FCSTD DOCUMENT  (FreeCAD 0.21R33771 (Git))
Label: RING2
License: All rights reserved
LicenseURL: http://en.wikipedia.org/wiki/All_rights_reserved
objects: Part::Part2DObjectPython×168, App::FeaturePython×24, App::DocumentObjectGroup×1
note: 168 computed .brp shape members not serialized (recipe doc carries the construction recipe); baked Part::Feature solids carry a one-line shape summary decoded from their .brp

FEATURE [Part::Part2DObjectPython] Rectangle  # Draft 2D object (typed FeaturePython)
  Area = 0
  ChamferSize = 0
  Columns = 1
  FilletRadius = 0
  Height = 6
  Length = 6
  MakeFace = false
  Placement = pos=(269.144,-43.1167,0) rot=(0,0,1;4.70122rad)
  Rows = 1
FEATURE [App::FeaturePython] Text  # WARN: FeaturePython — macro-defined, semantics opaque (R4)
  Placement = pos=(270.79,-53.3517,0) rot=(0,0,-1;4.73892rad)
  Text = 2
FEATURE [App::FeaturePython] Text001  # WARN: FeaturePython — macro-defined, semantics opaque (R4)
  Placement = pos=(268.047,49.5386,0) rot=(0,0,1;2.6241rad)
  Text = 6.
FEATURE [Part::Part2DObjectPython] Circle  # Draft 2D object (typed FeaturePython)
  Area = 1.13097
  FirstAngle = 0
  LastAngle = 0
  MakeFace = true
  Placement = pos=(272.07,-49.7498,0) rot=(0,0,1;4.70122rad)
  Radius = 0.6
FEATURE [Part::Part2DObjectPython] Rectangle001  # Draft 2D object (typed FeaturePython)
  Area = 0
  ChamferSize = 0
  Columns = 1
  FilletRadius = 0
  Height = 6
  Length = 6
  MakeFace = false
  Placement = pos=(270.385,-29.144,0) rot=(0,0,1;5.08397rad)
  Rows = 1
FEATURE [Part::Part2DObjectPython] Circle001  # Draft 2D object (typed FeaturePython)
  Area = 1.13097
  FirstAngle = 0
  LastAngle = 0
  MakeFace = true
  Placement = pos=(275.577,-34.2043,0) rot=(0,0,1;5.08397rad)
  Radius = 0.6
FEATURE [Part::Part2DObjectPython] Rectangle002  # Draft 2D object (typed FeaturePython)
  Area = 0
  ChamferSize = 0
  Columns = 1
  FilletRadius = 0
  Height = 6
  Length = 6
  MakeFace = false
  Placement = pos=(271.331,-15.2783,0) rot=(0,0,1;5.4573rad)
  Rows = 1
FEATURE [Part::Part2DObjectPython] Circle002  # Draft 2D object (typed FeaturePython)
  Area = 1.13097
  FirstAngle = 0
  LastAngle = 0
  MakeFace = true
  Placement = pos=(278.01,-18.0965,0) rot=(0,0,1;5.4573rad)
  Radius = 0.6
FEATURE [Part::Part2DObjectPython] Rectangle003  # Draft 2D object (typed FeaturePython)
  Area = 0
  ChamferSize = 0
  Columns = 1
  FilletRadius = 0
  Height = 6
  Length = 6
  MakeFace = false
  Placement = pos=(271.89,-1.0508,0) rot=(0,0,1;5.74807rad)
  Rows = 1
FEATURE [Part::Part2DObjectPython] Circle003  # Draft 2D object (typed FeaturePython)
  Area = 1.13097
  FirstAngle = 0
  LastAngle = 0
  MakeFace = true
  Placement = pos=(279.097,-1.83579,0) rot=(0,0,1;5.74807rad)
  Radius = 0.6
FEATURE [Part::Part2DObjectPython] Rectangle004  # Draft 2D object (typed FeaturePython)
  Area = 0
  ChamferSize = 0
  Columns = 1
  FilletRadius = 0
  Height = 6
  Length = 6
  MakeFace = false
  Placement = pos=(271.77,13.5629,0) rot=(0,0,1;5.95873rad)
  Rows = 1
FEATURE [Part::Part2DObjectPython] Circle004  # Draft 2D object (typed FeaturePython)
  Area = 1.13097
  FirstAngle = 0
  LastAngle = 0
  MakeFace = true
  Placement = pos=(278.982,14.3023,0) rot=(0,0,1;5.95873rad)
  Radius = 0.6
FEATURE [Part::Part2DObjectPython] Rectangle005  # Draft 2D object (typed FeaturePython)
  Area = 0
  ChamferSize = 0
  Columns = 1
  FilletRadius = 0
  Height = 6
  Length = 6
  MakeFace = false
  Placement = pos=(270.817,28.3851,0) rot=(0,0,1;6.11773rad)
  Rows = 1
FEATURE [Part::Part2DObjectPython] Circle005  # Draft 2D object (typed FeaturePython)
  Area = 1.13097
  FirstAngle = 0
  LastAngle = 0
  MakeFace = true
  Placement = pos=(277.821,30.2571,0) rot=(0,0,1;6.11773rad)
  Radius = 0.6
FEATURE [Part::Part2DObjectPython] Rectangle006  # Draft 2D object (typed FeaturePython)
  Area = 0
  ChamferSize = 0
  Columns = 1
  FilletRadius = 0
  Height = 6
  Length = 6
  MakeFace = false
  Placement = pos=(268.997,43.2674,0) rot=(0,0,1;6.24479rad)
  Rows = 1
FEATURE [Part::Part2DObjectPython] Circle006  # Draft 2D object (typed FeaturePython)
  Area = 1.13097
  FirstAngle = 0
  LastAngle = 0
  MakeFace = true
  Placement = pos=(275.707,46.0118,0) rot=(0,0,1;6.24479rad)
  Radius = 0.6
FEATURE [Part::Part2DObjectPython] Rectangle007  # Draft 2D object (typed FeaturePython)
  Area = 0
  ChamferSize = 0
  Columns = 1
  FilletRadius = 0
  Height = 6
  Length = 6
  MakeFace = false
  Placement = pos=(256.356,92.5739,0) rot=(0,0,1;0.191463rad)
  Rows = 1
FEATURE [App::FeaturePython] Text002  # WARN: FeaturePython — macro-defined, semantics opaque (R4)
  Placement = pos=(261.188,89.1931,0) rot=(0,0,-1;4.21532rad)
  Text = 2
FEATURE [App::FeaturePython] Text003  # WARN: FeaturePython — macro-defined, semantics opaque (R4)
  Placement = pos=(207.363,176.926,0) rot=(0,0,1;3.1477rad)
  Text = 7
FEATURE [Part::Part2DObjectPython] Circle007  # Draft 2D object (typed FeaturePython)
  Area = 1.13097
  FirstAngle = 0
  LastAngle = 0
  MakeFace = true
  Placement = pos=(262.264,96.7751,0) rot=(0,0,1;0.191463rad)
  Radius = 0.6
FEATURE [Part::Part2DObjectPython] Rectangle008  # Draft 2D object (typed FeaturePython)
  Area = 0
  ChamferSize = 0
  Columns = 1
  FilletRadius = 0
  Height = 6
  Length = 6
  MakeFace = false
  Placement = pos=(250.416,107.017,0) rot=(0,0,1;0.145211rad)
  Rows = 1
FEATURE [Part::Part2DObjectPython] Circle008  # Draft 2D object (typed FeaturePython)
  Area = 1.13097
  FirstAngle = 0
  LastAngle = 0
  MakeFace = true
  Placement = pos=(256.512,110.941,0) rot=(0,0,1;0.145211rad)
  Radius = 0.6
FEATURE [Part::Part2DObjectPython] Rectangle009  # Draft 2D object (typed FeaturePython)
  Area = 0
  ChamferSize = 0
  Columns = 1
  FilletRadius = 0
  Height = 6
  Length = 6
  MakeFace = false
  Placement = pos=(243.301,121.481,0) rot=(0,0,1;6.2598rad)
  Rows = 1
FEATURE [Part::Part2DObjectPython] Circle009  # Draft 2D object (typed FeaturePython)
  Area = 1.13097
  FirstAngle = 0
  LastAngle = 0
  MakeFace = true
  Placement = pos=(249.969,124.326,0) rot=(0,0,1;6.2598rad)
  Radius = 0.6
FEATURE [Part::Part2DObjectPython] Rectangle010  # Draft 2D object (typed FeaturePython)
  Area = 0
  ChamferSize = 0
  Columns = 1
  FilletRadius = 0
  Height = 6
  Length = 6
  MakeFace = false
  Placement = pos=(235.214,136.126,0) rot=(0,0,1;5.95541rad)
  Rows = 1
FEATURE [Part::Part2DObjectPython] Circle010  # Draft 2D object (typed FeaturePython)
  Area = 1.13097
  FirstAngle = 0
  LastAngle = 0
  MakeFace = true
  Placement = pos=(242.428,136.841,0) rot=(0,0,1;5.95541rad)
  Radius = 0.6
FEATURE [Part::Part2DObjectPython] Rectangle011  # Draft 2D object (typed FeaturePython)
  Area = 0
  ChamferSize = 0
  Columns = 1
  FilletRadius = 0
  Height = 6
  Length = 6
  MakeFace = false
  Placement = pos=(226.732,150.48,0) rot=(0,0,1;5.65871rad)
  Rows = 1
FEATURE [Part::Part2DObjectPython] Circle011  # Draft 2D object (typed FeaturePython)
  Area = 1.13097
  FirstAngle = 0
  LastAngle = 0
  MakeFace = true
  Placement = pos=(233.841,149.055,0) rot=(0,0,1;5.65871rad)
  Radius = 0.6
FEATURE [Part::Part2DObjectPython] Rectangle012  # Draft 2D object (typed FeaturePython)
  Area = 0
  ChamferSize = 0
  Columns = 1
  FilletRadius = 0
  Height = 6
  Length = 6
  MakeFace = false
  Placement = pos=(217.857,163.826,0) rot=(0,0,1;5.50337rad)
  Rows = 1
FEATURE [Part::Part2DObjectPython] Circle012  # Draft 2D object (typed FeaturePython)
  Area = 1.13097
  FirstAngle = 0
  LastAngle = 0
  MakeFace = true
  Placement = pos=(224.66,161.319,0) rot=(0,0,1;5.50337rad)
  Radius = 0.6
FEATURE [Part::Part2DObjectPython] Rectangle013  # Draft 2D object (typed FeaturePython)
  Area = 0
  ChamferSize = 0
  Columns = 1
  FilletRadius = 0
  Height = 6
  Length = 6
  MakeFace = false
  Placement = pos=(208.339,176.143,0) rot=(0,0,1;5.46882rad)
  Rows = 1
FEATURE [Part::Part2DObjectPython] Circle013  # Draft 2D object (typed FeaturePython)
  Area = 1.13097
  FirstAngle = 0
  LastAngle = 0
  MakeFace = true
  Placement = pos=(215.051,173.402,0) rot=(0,0,1;5.46882rad)
  Radius = 0.6
FEATURE [Part::Part2DObjectPython] Rectangle014  # Draft 2D object (typed FeaturePython)
  Area = 0
  ChamferSize = 0
  Columns = 1
  FilletRadius = 0
  Height = 6
  Length = 6
  MakeFace = false
  Placement = pos=(171.868,211.706,0) rot=(0,0,1;5.70531rad)
  Rows = 1
FEATURE [App::FeaturePython] Text004  # WARN: FeaturePython — macro-defined, semantics opaque (R4)
  Placement = pos=(181.597,207.836,0) rot=(0,0,-1;3.69172rad)
  Text = 2
FEATURE [App::FeaturePython] Text005  # WARN: FeaturePython — macro-defined, semantics opaque (R4)
  Placement = pos=(91.1209,256.902,0) rot=(0,0,1;3.6713rad)
  Text = 8
FEATURE [Part::Part2DObjectPython] Circle014  # Draft 2D object (typed FeaturePython)
  Area = 1.13097
  FirstAngle = 0
  LastAngle = 0
  MakeFace = true
  Placement = pos=(179.035,210.614,0) rot=(0,0,1;5.70531rad)
  Radius = 0.6
FEATURE [Part::Part2DObjectPython] Rectangle015  # Draft 2D object (typed FeaturePython)
  Area = 0
  ChamferSize = 0
  Columns = 1
  FilletRadius = 0
  Height = 6
  Length = 6
  MakeFace = false
  Placement = pos=(159.811,220.802,0) rot=(0,0,1;5.80863rad)
  Rows = 1
FEATURE [Part::Part2DObjectPython] Circle015  # Draft 2D object (typed FeaturePython)
  Area = 1.13097
  FirstAngle = 0
  LastAngle = 0
  MakeFace = true
  Placement = pos=(167.052,220.455,0) rot=(0,0,1;5.80863rad)
  Radius = 0.6
FEATURE [Part::Part2DObjectPython] Rectangle016  # Draft 2D object (typed FeaturePython)
  Area = 0
  ChamferSize = 0
  Columns = 1
  FilletRadius = 0
  Height = 6
  Length = 6
  MakeFace = false
  Placement = pos=(147.277,229.211,0) rot=(0,0,1;5.91248rad)
  Rows = 1
FEATURE [Part::Part2DObjectPython] Circle016  # Draft 2D object (typed FeaturePython)
  Area = 1.13097
  FirstAngle = 0
  LastAngle = 0
  MakeFace = true
  Placement = pos=(154.515,229.616,0) rot=(0,0,1;5.91248rad)
  Radius = 0.6
FEATURE [Part::Part2DObjectPython] Rectangle017  # Draft 2D object (typed FeaturePython)
  Area = 0
  ChamferSize = 0
  Columns = 1
  FilletRadius = 0
  Height = 6
  Length = 6
  MakeFace = false
  Placement = pos=(134.314,236.919,0) rot=(0,0,1;6.0158rad)
  Rows = 1
FEATURE [Part::Part2DObjectPython] Circle017  # Draft 2D object (typed FeaturePython)
  Area = 1.13097
  FirstAngle = 0
  LastAngle = 0
  MakeFace = true
  Placement = pos=(141.472,238.069,0) rot=(0,0,1;6.0158rad)
  Radius = 0.6
FEATURE [Part::Part2DObjectPython] Rectangle018  # Draft 2D object (typed FeaturePython)
  Area = 0
  ChamferSize = 0
  Columns = 1
  FilletRadius = 0
  Height = 6
  Length = 6
  MakeFace = false
  Placement = pos=(120.961,243.9,0) rot=(0,0,1;6.1193rad)
  Rows = 1
FEATURE [Part::Part2DObjectPython] Circle018  # Draft 2D object (typed FeaturePython)
  Area = 1.13097
  FirstAngle = 0
  LastAngle = 0
  MakeFace = true
  Placement = pos=(127.962,245.783,0) rot=(0,0,1;6.1193rad)
  Radius = 0.6
FEATURE [Part::Part2DObjectPython] Rectangle019  # Draft 2D object (typed FeaturePython)
  Area = 0
  ChamferSize = 0
  Columns = 1
  FilletRadius = 0
  Height = 6
  Length = 6
  MakeFace = false
  Placement = pos=(107.269,250.109,0) rot=(0,0,1;6.23152rad)
  Rows = 1
FEATURE [Part::Part2DObjectPython] Circle019  # Draft 2D object (typed FeaturePython)
  Area = 1.13097
  FirstAngle = 0
  LastAngle = 0
  MakeFace = true
  Placement = pos=(114.015,252.764,0) rot=(0,0,1;6.23152rad)
  Radius = 0.6
FEATURE [Part::Part2DObjectPython] Rectangle020  # Draft 2D object (typed FeaturePython)
  Area = 0
  ChamferSize = 0
  Columns = 1
  FilletRadius = 0
  Height = 6
  Length = 6
  MakeFace = false
  Placement = pos=(93.3516,255.489,0) rot=(0,0,1;0.083776rad)
  Rows = 1
FEATURE [Part::Part2DObjectPython] Circle020  # Draft 2D object (typed FeaturePython)
  Area = 1.13097
  FirstAngle = 0
  LastAngle = 0
  MakeFace = true
  Placement = pos=(99.6774,259.031,0) rot=(0,0,1;0.083776rad)
  Radius = 0.6
FEATURE [Part::Part2DObjectPython] Rectangle021  # Draft 2D object (typed FeaturePython)
  Area = 0
  ChamferSize = 0
  Columns = 1
  FilletRadius = 0
  Height = 6
  Length = 6
  MakeFace = false
  Placement = pos=(48.0649,268.324,0) rot=(0,0,1;1.25367rad)
  Rows = 1
FEATURE [App::FeaturePython] Text006  # WARN: FeaturePython — macro-defined, semantics opaque (R4)
  Placement = pos=(53.3517,270.79,0) rot=(0,0,-1;3.16812rad)
  Text = 2
FEATURE [App::FeaturePython] Text007  # WARN: FeaturePython — macro-defined, semantics opaque (R4)
  Placement = pos=(-49.5386,268.047,0) rot=(0,0,1;4.1949rad)
  Text = 9
FEATURE [Part::Part2DObjectPython] Circle021  # Draft 2D object (typed FeaturePython)
  Area = 1.13097
  FirstAngle = 0
  LastAngle = 0
  MakeFace = true
  Placement = pos=(47.2726,275.53,0) rot=(0,0,1;1.25367rad)
  Radius = 0.6
FEATURE [Part::Part2DObjectPython] Rectangle022  # Draft 2D object (typed FeaturePython)
  Area = 0
  ChamferSize = 0
  Columns = 1
  FilletRadius = 0
  Height = 6
  Length = 6
  MakeFace = false
  Placement = pos=(34.7405,272.578,0) rot=(0,0,1;1.94587rad)
  Rows = 1
FEATURE [Part::Part2DObjectPython] Circle022  # Draft 2D object (typed FeaturePython)
  Area = 1.13097
  FirstAngle = 0
  LastAngle = 0
  MakeFace = true
  Placement = pos=(29.5312,277.62,0) rot=(0,0,1;1.94587rad)
  Radius = 0.6
FEATURE [Part::Part2DObjectPython] Rectangle023  # Draft 2D object (typed FeaturePython)
  Area = 0
  ChamferSize = 0
  Columns = 1
  FilletRadius = 0
  Height = 6
  Length = 6
  MakeFace = false
  Placement = pos=(19.6498,276.171,0) rot=(0,0,1;2.49844rad)
  Rows = 1
FEATURE [Part::Part2DObjectPython] Circle023  # Draft 2D object (typed FeaturePython)
  Area = 1.13097
  FirstAngle = 0
  LastAngle = 0
  MakeFace = true
  Placement = pos=(12.5693,277.729,0) rot=(0,0,1;2.49844rad)
  Radius = 0.6
FEATURE [Part::Part2DObjectPython] Rectangle024  # Draft 2D object (typed FeaturePython)
  Area = 0
  ChamferSize = 0
  Columns = 1
  FilletRadius = 0
  Height = 6
  Length = 6
  MakeFace = false
  Placement = pos=(3.67238,278.125,0) rot=(0,0,1;2.88067rad)
  Rows = 1
FEATURE [Part::Part2DObjectPython] Circle024  # Draft 2D object (typed FeaturePython)
  Area = 1.13097
  FirstAngle = 0
  LastAngle = 0
  MakeFace = true
  Placement = pos=(-3.47814,276.929,0) rot=(0,0,1;2.88067rad)
  Radius = 0.6
FEATURE [Part::Part2DObjectPython] Rectangle025  # Draft 2D object (typed FeaturePython)
  Area = 0
  ChamferSize = 0
  Columns = 1
  FilletRadius = 0
  Height = 6
  Length = 6
  MakeFace = false
  Placement = pos=(-12.4484,278.568,0) rot=(0,0,1;3.14107rad)
  Rows = 1
FEATURE [Part::Part2DObjectPython] Circle025  # Draft 2D object (typed FeaturePython)
  Area = 1.13097
  FirstAngle = 0
  LastAngle = 0
  MakeFace = true
  Placement = pos=(-19.05,275.572,0) rot=(0,0,1;3.14107rad)
  Radius = 0.6
FEATURE [Part::Part2DObjectPython] Rectangle026  # Draft 2D object (typed FeaturePython)
  Area = 0
  ChamferSize = 0
  Columns = 1
  FilletRadius = 0
  Height = 6
  Length = 6
  MakeFace = false
  Placement = pos=(-27.849,277.269,0) rot=(0,0,1;3.14124rad)
  Rows = 1
FEATURE [Part::Part2DObjectPython] Circle026  # Draft 2D object (typed FeaturePython)
  Area = 1.13097
  FirstAngle = 0
  LastAngle = 0
  MakeFace = true
  Placement = pos=(-34.45,274.271,0) rot=(0,0,1;3.14124rad)
  Radius = 0.6
FEATURE [Part::Part2DObjectPython] Rectangle027  # Draft 2D object (typed FeaturePython)
  Area = 0
  ChamferSize = 0
  Columns = 1
  FilletRadius = 0
  Height = 6
  Length = 6
  MakeFace = false
  Placement = pos=(-43.15,275.11,0) rot=(0,0,1;3.14159rad)
  Rows = 1
FEATURE [Part::Part2DObjectPython] Circle027  # Draft 2D object (typed FeaturePython)
  Area = 1.13097
  FirstAngle = 0
  LastAngle = 0
  MakeFace = true
  Placement = pos=(-49.75,272.11,0) rot=(0,0,1;3.14159rad)
  Radius = 0.6
FEATURE [Part::Part2DObjectPython] Rectangle028  # Draft 2D object (typed FeaturePython)
  Area = 0
  ChamferSize = 0
  Columns = 1
  FilletRadius = 0
  Height = 6
  Length = 6
  MakeFace = false
  Placement = pos=(-93.09,261.73,0) rot=(0,0,1;3.14159rad)
  Rows = 1
FEATURE [App::FeaturePython] Text008  # WARN: FeaturePython — macro-defined, semantics opaque (R4)
  Placement = pos=(-89.1931,261.188,0) rot=(0,0,-1;2.64452rad)
  Text = 2
FEATURE [App::FeaturePython] Text009  # WARN: FeaturePython — macro-defined, semantics opaque (R4)
  Placement = pos=(-176.926,207.363,0) rot=(0,0,1;4.7185rad)
  Text = 10
FEATURE [Part::Part2DObjectPython] Circle028  # Draft 2D object (typed FeaturePython)
  Area = 1.13097
  FirstAngle = 0
  LastAngle = 0
  MakeFace = true
  Placement = pos=(-99.69,258.73,0) rot=(0,0,1;3.14159rad)
  Radius = 0.6
FEATURE [Part::Part2DObjectPython] Rectangle029  # Draft 2D object (typed FeaturePython)
  Area = 0
  ChamferSize = 0
  Columns = 1
  FilletRadius = 0
  Height = 6
  Length = 6
  MakeFace = false
  Placement = pos=(-107.42,255.95,0) rot=(0,0,1;3.14159rad)
  Rows = 1
FEATURE [Part::Part2DObjectPython] Circle029  # Draft 2D object (typed FeaturePython)
  Area = 1.13097
  FirstAngle = 0
  LastAngle = 0
  MakeFace = true
  Placement = pos=(-114.02,252.95,0) rot=(0,0,1;3.14159rad)
  Radius = 0.6
FEATURE [Part::Part2DObjectPython] Rectangle030  # Draft 2D object (typed FeaturePython)
  Area = 0
  ChamferSize = 0
  Columns = 1
  FilletRadius = 0
  Height = 6
  Length = 6
  MakeFace = false
  Placement = pos=(-125.426,250.489,0) rot=(0,0,1;4.16889rad)
  Rows = 1
FEATURE [Part::Part2DObjectPython] Circle030  # Draft 2D object (typed FeaturePython)
  Area = 1.13097
  FirstAngle = 0
  LastAngle = 0
  MakeFace = true
  Placement = pos=(-126.272,243.289,0) rot=(0,0,1;4.16889rad)
  Radius = 0.6
FEATURE [Part::Part2DObjectPython] Rectangle031  # Draft 2D object (typed FeaturePython)
  Area = 0
  ChamferSize = 0
  Columns = 1
  FilletRadius = 0
  Height = 6
  Length = 6
  MakeFace = false
  Placement = pos=(-138.447,243.239,0) rot=(0,0,1;4.03258rad)
  Rows = 1
FEATURE [Part::Part2DObjectPython] Circle031  # Draft 2D object (typed FeaturePython)
  Area = 1.13097
  FirstAngle = 0
  LastAngle = 0
  MakeFace = true
  Placement = pos=(-140.263,236.22,0) rot=(0,0,1;4.03258rad)
  Radius = 0.6
FEATURE [Part::Part2DObjectPython] Rectangle032  # Draft 2D object (typed FeaturePython)
  Area = 0
  ChamferSize = 0
  Columns = 1
  FilletRadius = 0
  Height = 6
  Length = 6
  MakeFace = false
  Placement = pos=(-148.16,233.92,0) rot=(0,0,1;3.14159rad)
  Rows = 1
FEATURE [Part::Part2DObjectPython] Circle032  # Draft 2D object (typed FeaturePython)
  Area = 1.13097
  FirstAngle = 0
  LastAngle = 0
  MakeFace = true
  Placement = pos=(-154.76,230.92,0) rot=(0,0,1;3.14159rad)
  Radius = 0.6
FEATURE [Part::Part2DObjectPython] Rectangle033  # Draft 2D object (typed FeaturePython)
  Area = 0
  ChamferSize = 0
  Columns = 1
  FilletRadius = 0
  Height = 6
  Length = 6
  MakeFace = false
  Placement = pos=(-161.861,225.847,0) rot=(0,0,1;3.439rad)
  Rows = 1
FEATURE [Part::Part2DObjectPython] Circle033  # Draft 2D object (typed FeaturePython)
  Area = 1.13097
  FirstAngle = 0
  LastAngle = 0
  MakeFace = true
  Placement = pos=(-167.292,221.045,0) rot=(0,0,1;3.439rad)
  Radius = 0.6
FEATURE [Part::Part2DObjectPython] Rectangle034  # Draft 2D object (typed FeaturePython)
  Area = 0
  ChamferSize = 0
  Columns = 1
  FilletRadius = 0
  Height = 6
  Length = 6
  MakeFace = false
  Placement = pos=(-173.325,215.857,0) rot=(0,0,1;3.23863rad)
  Rows = 1
FEATURE [Part::Part2DObjectPython] Circle034  # Draft 2D object (typed FeaturePython)
  Area = 1.13097
  FirstAngle = 0
  LastAngle = 0
  MakeFace = true
  Placement = pos=(-179.603,212.231,0) rot=(0,0,1;3.23863rad)
  Radius = 0.6
FEATURE [Part::Part2DObjectPython] Rectangle035  # Draft 2D object (typed FeaturePython)
  Area = 0
  ChamferSize = 0
  Columns = 1
  FilletRadius = 0
  Height = 6
  Length = 6
  MakeFace = false
  Placement = pos=(-209.548,178.988,0) rot=(0,0,1;3.13095rad)
  Rows = 1
FEATURE [App::FeaturePython] Text010  # WARN: FeaturePython — macro-defined, semantics opaque (R4)
  Placement = pos=(-207.836,181.597,0) rot=(0,0,-1;2.12092rad)
  Text = 2
FEATURE [App::FeaturePython] Text011  # WARN: FeaturePython — macro-defined, semantics opaque (R4)
  Placement = pos=(-256.902,91.1209,0) rot=(0,0,1;5.2421rad)
  Text = 11
FEATURE [Part::Part2DObjectPython] Circle035  # Draft 2D object (typed FeaturePython)
  Area = 1.13097
  FirstAngle = 0
  LastAngle = 0
  MakeFace = true
  Placement = pos=(-216.18,176.058,0) rot=(0,0,1;3.13095rad)
  Radius = 0.6
FEATURE [Part::Part2DObjectPython] Rectangle036  # Draft 2D object (typed FeaturePython)
  Area = 0
  ChamferSize = 0
  Columns = 1
  FilletRadius = 0
  Height = 6
  Length = 6
  MakeFace = false
  Placement = pos=(-219.095,166.845,0) rot=(0,0,1;3.14002rad)
  Rows = 1
FEATURE [Part::Part2DObjectPython] Circle036  # Draft 2D object (typed FeaturePython)
  Area = 1.13097
  FirstAngle = 0
  LastAngle = 0
  MakeFace = true
  Placement = pos=(-225.7,163.856,0) rot=(0,0,1;3.14002rad)
  Radius = 0.6
FEATURE [Part::Part2DObjectPython] Rectangle037  # Draft 2D object (typed FeaturePython)
  Area = 0
  ChamferSize = 0
  Columns = 1
  FilletRadius = 0
  Height = 6
  Length = 6
  MakeFace = false
  Placement = pos=(-228.336,154.525,0) rot=(0,0,1;3.27214rad)
  Rows = 1
FEATURE [Part::Part2DObjectPython] Circle037  # Draft 2D object (typed FeaturePython)
  Area = 1.13097
  FirstAngle = 0
  LastAngle = 0
  MakeFace = true
  Placement = pos=(-234.489,150.691,0) rot=(0,0,1;3.27214rad)
  Radius = 0.6
FEATURE [Part::Part2DObjectPython] Rectangle038  # Draft 2D object (typed FeaturePython)
  Area = 0
  ChamferSize = 0
  Columns = 1
  FilletRadius = 0
  Height = 6
  Length = 6
  MakeFace = false
  Placement = pos=(-236.588,141.476,0) rot=(0,0,1;3.31648rad)
  Rows = 1
FEATURE [Part::Part2DObjectPython] Circle038  # Draft 2D object (typed FeaturePython)
  Area = 1.13097
  FirstAngle = 0
  LastAngle = 0
  MakeFace = true
  Placement = pos=(-242.565,137.374,0) rot=(0,0,1;3.31648rad)
  Radius = 0.6
FEATURE [Part::Part2DObjectPython] Rectangle039  # Draft 2D object (typed FeaturePython)
  Area = 0
  ChamferSize = 0
  Columns = 1
  FilletRadius = 0
  Height = 6
  Length = 6
  MakeFace = false
  Placement = pos=(-244.059,127.968,0) rot=(0,0,1;3.35086rad)
  Rows = 1
FEATURE [Part::Part2DObjectPython] Circle039  # Draft 2D object (typed FeaturePython)
  Area = 1.13097
  FirstAngle = 0
  LastAngle = 0
  MakeFace = true
  Placement = pos=(-249.891,123.662,0) rot=(0,0,1;3.35086rad)
  Radius = 0.6
FEATURE [Part::Part2DObjectPython] Rectangle040  # Draft 2D object (typed FeaturePython)
  Area = 0
  ChamferSize = 0
  Columns = 1
  FilletRadius = 0
  Height = 6
  Length = 6
  MakeFace = false
  Placement = pos=(-250.711,114.024,0) rot=(0,0,1;3.3711rad)
  Rows = 1
FEATURE [Part::Part2DObjectPython] Circle040  # Draft 2D object (typed FeaturePython)
  Area = 1.13097
  FirstAngle = 0
  LastAngle = 0
  MakeFace = true
  Placement = pos=(-256.456,109.601,0) rot=(0,0,1;3.3711rad)
  Radius = 0.6
FEATURE [Part::Part2DObjectPython] Rectangle041  # Draft 2D object (typed FeaturePython)
  Area = 0
  ChamferSize = 0
  Columns = 1
  FilletRadius = 0
  Height = 6
  Length = 6
  MakeFace = false
  Placement = pos=(-256.482,99.6884,0) rot=(0,0,1;3.36866rad)
  Rows = 1
FEATURE [Part::Part2DObjectPython] Circle041  # Draft 2D object (typed FeaturePython)
  Area = 1.13097
  FirstAngle = 0
  LastAngle = 0
  MakeFace = true
  Placement = pos=(-262.238,95.2796,0) rot=(0,0,1;3.36866rad)
  Radius = 0.6
FEATURE [Part::Part2DObjectPython] Rectangle042  # Draft 2D object (typed FeaturePython)
  Area = 0
  ChamferSize = 0
  Columns = 1
  FilletRadius = 0
  Height = 6
  Length = 6
  MakeFace = false
  Placement = pos=(-269.081,49.1211,0) rot=(0,0,1;3.13199rad)
  Rows = 1
FEATURE [App::FeaturePython] Text012  # WARN: FeaturePython — macro-defined, semantics opaque (R4)
  Placement = pos=(-270.79,53.3517,0) rot=(0,0,-1;1.59733rad)
  Text = 2
FEATURE [App::FeaturePython] Text013  # WARN: FeaturePython — macro-defined, semantics opaque (R4)
  Placement = pos=(-268.047,-49.5386,0) rot=(0,0,1;5.7657rad)
  Text = 12
FEATURE [Part::Part2DObjectPython] Circle042  # Draft 2D object (typed FeaturePython)
  Area = 1.13097
  FirstAngle = 0
  LastAngle = 0
  MakeFace = true
  Placement = pos=(-275.71,46.1846,0) rot=(0,0,1;3.13199rad)
  Radius = 0.6
FEATURE [Part::Part2DObjectPython] Rectangle043  # Draft 2D object (typed FeaturePython)
  Area = 0
  ChamferSize = 0
  Columns = 1
  FilletRadius = 0
  Height = 6
  Length = 6
  MakeFace = false
  Placement = pos=(-271.382,33.9584,0) rot=(0,0,1;3.17842rad)
  Rows = 1
FEATURE [Part::Part2DObjectPython] Circle043  # Draft 2D object (typed FeaturePython)
  Area = 1.13097
  FirstAngle = 0
  LastAngle = 0
  MakeFace = true
  Placement = pos=(-277.868,30.7175,0) rot=(0,0,1;3.17842rad)
  Radius = 0.6
FEATURE [Part::Part2DObjectPython] Rectangle044  # Draft 2D object (typed FeaturePython)
  Area = 0
  ChamferSize = 0
  Columns = 1
  FilletRadius = 0
  Height = 6
  Length = 6
  MakeFace = false
  Placement = pos=(-272.32,18.1771,0) rot=(0,0,1;3.05433rad)
  Rows = 1
FEATURE [Part::Part2DObjectPython] Circle044  # Draft 2D object (typed FeaturePython)
  Area = 1.13097
  FirstAngle = 0
  LastAngle = 0
  MakeFace = true
  Placement = pos=(-279.156,15.7638,0) rot=(0,0,1;3.05433rad)
  Radius = 0.6
FEATURE [Part::Part2DObjectPython] Rectangle045  # Draft 2D object (typed FeaturePython)
  Area = 0
  ChamferSize = 0
  Columns = 1
  FilletRadius = 0
  Height = 6
  Length = 6
  MakeFace = false
  Placement = pos=(-279.273,2.69922,0) rot=(0,0,1;4.80821rad)
  Rows = 1
FEATURE [Part::Part2DObjectPython] Circle045  # Draft 2D object (typed FeaturePython)
  Area = 1.13097
  FirstAngle = 0
  LastAngle = 0
  MakeFace = true
  Placement = pos=(-275.656,-3.58349,0) rot=(0,0,1;4.80821rad)
  Radius = 0.6
FEATURE [Part::Part2DObjectPython] Rectangle046  # Draft 2D object (typed FeaturePython)
  Area = 0
  ChamferSize = 0
  Columns = 1
  FilletRadius = 0
  Height = 6
  Length = 6
  MakeFace = false
  Placement = pos=(-279.129,-17.7588,0) rot=(0,0,1;6.07322rad)
  Rows = 1
FEATURE [Part::Part2DObjectPython] Circle046  # Draft 2D object (typed FeaturePython)
  Area = 1.13097
  FirstAngle = 0
  LastAngle = 0
  MakeFace = true
  Placement = pos=(-272.049,-16.2003,0) rot=(0,0,1;6.07322rad)
  Radius = 0.6
FEATURE [Part::Part2DObjectPython] Rectangle047  # Draft 2D object (typed FeaturePython)
  Area = 0
  ChamferSize = 0
  Columns = 1
  FilletRadius = 0
  Height = 6
  Length = 6
  MakeFace = false
  Placement = pos=(-277.649,-33.4157,0) rot=(0,0,1;6.14722rad)
  Rows = 1
FEATURE [Part::Part2DObjectPython] Circle047  # Draft 2D object (typed FeaturePython)
  Area = 1.13097
  FirstAngle = 0
  LastAngle = 0
  MakeFace = true
  Placement = pos=(-270.703,-31.338,0) rot=(0,0,1;6.14722rad)
  Radius = 0.6
FEATURE [Part::Part2DObjectPython] Rectangle048  # Draft 2D object (typed FeaturePython)
  Area = 0
  ChamferSize = 0
  Columns = 1
  FilletRadius = 0
  Height = 6
  Length = 6
  MakeFace = false
  Placement = pos=(-275.342,-48.8986,0) rot=(0,0,1;6.20255rad)
  Rows = 1
FEATURE [Part::Part2DObjectPython] Circle048  # Draft 2D object (typed FeaturePython)
  Area = 1.13097
  FirstAngle = 0
  LastAngle = 0
  MakeFace = true
  Placement = pos=(-268.522,-46.44,0) rot=(0,0,1;6.20255rad)
  Radius = 0.6
FEATURE [Part::Part2DObjectPython] Rectangle049  # Draft 2D object (typed FeaturePython)
  Area = 0
  ChamferSize = 0
  Columns = 1
  FilletRadius = 0
  Height = 6
  Length = 6
  MakeFace = false
  Placement = pos=(-261.324,-99.4469,0) rot=(0,0,1;0.127409rad)
  Rows = 1
FEATURE [App::FeaturePython] Text014  # WARN: FeaturePython — macro-defined, semantics opaque (R4)
  Placement = pos=(-261.188,-89.1931,0) rot=(0,0,-1;1.07373rad)
  Text = 2
FEATURE [App::FeaturePython] Text015  # WARN: FeaturePython — macro-defined, semantics opaque (R4)
  Placement = pos=(-207.363,-176.926,0) rot=(0,0,-1;6.27708rad)
  Text = 1
FEATURE [Part::Part2DObjectPython] Circle049  # Draft 2D object (typed FeaturePython)
  Area = 1.13097
  FirstAngle = 0
  LastAngle = 0
  MakeFace = true
  Placement = pos=(-255.159,-95.6326,0) rot=(0,0,1;0.127409rad)
  Radius = 0.6
FEATURE [Part::Part2DObjectPython] Rectangle050  # Draft 2D object (typed FeaturePython)
  Area = 0
  ChamferSize = 0
  Columns = 1
  FilletRadius = 0
  Height = 6
  Length = 6
  MakeFace = false
  Placement = pos=(-255.327,-113.934,0) rot=(0,0,1;0.190764rad)
  Rows = 1
FEATURE [Part::Part2DObjectPython] Circle050  # Draft 2D object (typed FeaturePython)
  Area = 1.13097
  FirstAngle = 0
  LastAngle = 0
  MakeFace = true
  Placement = pos=(-249.415,-109.737,0) rot=(0,0,1;0.190764rad)
  Radius = 0.6
FEATURE [Part::Part2DObjectPython] Rectangle051  # Draft 2D object (typed FeaturePython)
  Area = 0
  ChamferSize = 0
  Columns = 1
  FilletRadius = 0
  Height = 6
  Length = 6
  MakeFace = false
  Placement = pos=(-248.517,-128.069,0) rot=(0,0,1;0.254818rad)
  Rows = 1
FEATURE [Part::Part2DObjectPython] Circle051  # Draft 2D object (typed FeaturePython)
  Area = 1.13097
  FirstAngle = 0
  LastAngle = 0
  MakeFace = true
  Placement = pos=(-242.886,-123.503,0) rot=(0,0,1;0.254818rad)
  Radius = 0.6
FEATURE [Part::Part2DObjectPython] Rectangle052  # Draft 2D object (typed FeaturePython)
  Area = 0
  ChamferSize = 0
  Columns = 1
  FilletRadius = 0
  Height = 6
  Length = 6
  MakeFace = false
  Placement = pos=(-240.932,-141.788,0) rot=(0,0,1;0.317999rad)
  Rows = 1
FEATURE [Part::Part2DObjectPython] Circle052  # Draft 2D object (typed FeaturePython)
  Area = 1.13097
  FirstAngle = 0
  LastAngle = 0
  MakeFace = true
  Placement = pos=(-235.6,-136.874,0) rot=(0,0,1;0.317999rad)
  Radius = 0.6
FEATURE [Part::Part2DObjectPython] Rectangle053  # Draft 2D object (typed FeaturePython)
  Area = 0
  ChamferSize = 0
  Columns = 1
  FilletRadius = 0
  Height = 6
  Length = 6
  MakeFace = false
  Placement = pos=(-232.589,-155.06,0) rot=(0,0,1;0.381005rad)
  Rows = 1
FEATURE [Part::Part2DObjectPython] Circle053  # Draft 2D object (typed FeaturePython)
  Area = 1.13097
  FirstAngle = 0
  LastAngle = 0
  MakeFace = true
  Placement = pos=(-227.578,-149.821,0) rot=(0,0,1;0.381005rad)
  Radius = 0.6
FEATURE [Part::Part2DObjectPython] Rectangle054  # Draft 2D object (typed FeaturePython)
  Area = 0
  ChamferSize = 0
  Columns = 1
  FilletRadius = 0
  Height = 6
  Length = 6
  MakeFace = false
  Placement = pos=(-223.523,-167.847,0) rot=(0,0,1;0.443488rad)
  Rows = 1
FEATURE [Part::Part2DObjectPython] Circle054  # Draft 2D object (typed FeaturePython)
  Area = 1.13097
  FirstAngle = 0
  LastAngle = 0
  MakeFace = true
  Placement = pos=(-218.848,-162.305,0) rot=(0,0,1;0.443488rad)
  Radius = 0.6
FEATURE [Part::Part2DObjectPython] Rectangle055  # Draft 2D object (typed FeaturePython)
  Area = 0
  ChamferSize = 0
  Columns = 1
  FilletRadius = 0
  Height = 6
  Length = 6
  MakeFace = false
  Placement = pos=(-213.757,-180.096,0) rot=(0,0,1;0.5044rad)
  Rows = 1
FEATURE [Part::Part2DObjectPython] Circle055  # Draft 2D object (typed FeaturePython)
  Area = 1.13097
  FirstAngle = 0
  LastAngle = 0
  MakeFace = true
  Placement = pos=(-209.428,-174.28,0) rot=(0,0,1;0.5044rad)
  Radius = 0.6
FEATURE [Part::Part2DObjectPython] Rectangle056  # Draft 2D object (typed FeaturePython)
  Area = 0
  ChamferSize = 0
  Columns = 1
  FilletRadius = 0
  Height = 6
  Length = 6
  MakeFace = false
  Placement = pos=(-176.938,-216.722,0) rot=(0,0,1;0.567407rad)
  Rows = 1
FEATURE [App::FeaturePython] Text016  # WARN: FeaturePython — macro-defined, semantics opaque (R4)
  Placement = pos=(-181.597,-207.836,0) rot=(0,0,-1;0.550128rad)
  Text = 2
FEATURE [App::FeaturePython] Text017  # WARN: FeaturePython — macro-defined, semantics opaque (R4)
  Placement = pos=(-91.1209,-256.902,0) rot=(0,0,-1;5.75348rad)
  Text = 2
FEATURE [Part::Part2DObjectPython] Circle056  # Draft 2D object (typed FeaturePython)
  Area = 1.13097
  FirstAngle = 0
  LastAngle = 0
  MakeFace = true
  Placement = pos=(-172.984,-210.645,0) rot=(0,0,1;0.567407rad)
  Radius = 0.6
FEATURE [Part::Part2DObjectPython] Rectangle057  # Draft 2D object (typed FeaturePython)
  Area = 0
  ChamferSize = 0
  Columns = 1
  FilletRadius = 0
  Height = 6
  Length = 6
  MakeFace = false
  Placement = pos=(-165.977,-225.771,0) rot=(0,0,1;0.260229rad)
  Rows = 1
FEATURE [Part::Part2DObjectPython] Circle057  # Draft 2D object (typed FeaturePython)
  Area = 1.13097
  FirstAngle = 0
  LastAngle = 0
  MakeFace = true
  Placement = pos=(-160.371,-221.174,0) rot=(0,0,1;0.260229rad)
  Radius = 0.6
FEATURE [Part::Part2DObjectPython] Rectangle058  # Draft 2D object (typed FeaturePython)
  Area = 0
  ChamferSize = 0
  Columns = 1
  FilletRadius = 0
  Height = 6
  Length = 6
  MakeFace = false
  Placement = pos=(-155.393,-231.201,0) rot=(0,0,1;5.56411rad)
  Rows = 1
FEATURE [Part::Part2DObjectPython] Circle058  # Draft 2D object (typed FeaturePython)
  Area = 1.13097
  FirstAngle = 0
  LastAngle = 0
  MakeFace = true
  Placement = pos=(-148.451,-233.291,0) rot=(0,0,1;5.56411rad)
  Radius = 0.6
FEATURE [Part::Part2DObjectPython] Rectangle059  # Draft 2D object (typed FeaturePython)
  Area = 0
  ChamferSize = 0
  Columns = 1
  FilletRadius = 0
  Height = 6
  Length = 6
  MakeFace = false
  Placement = pos=(-141.889,-237.323,0) rot=(0,0,1;5.08641rad)
  Rows = 1
FEATURE [Part::Part2DObjectPython] Circle059  # Draft 2D object (typed FeaturePython)
  Area = 1.13097
  FirstAngle = 0
  LastAngle = 0
  MakeFace = true
  Placement = pos=(-136.685,-242.371,0) rot=(0,0,1;5.08641rad)
  Radius = 0.6
FEATURE [Part::Part2DObjectPython] Rectangle060  # Draft 2D object (typed FeaturePython)
  Area = 0
  ChamferSize = 0
  Columns = 1
  FilletRadius = 0
  Height = 6
  Length = 6
  MakeFace = false
  Placement = pos=(-128.219,-244.502,0) rot=(0,0,1;5.04173rad)
  Rows = 1
FEATURE [Part::Part2DObjectPython] Circle060  # Draft 2D object (typed FeaturePython)
  Area = 1.13097
  FirstAngle = 0
  LastAngle = 0
  MakeFace = true
  Placement = pos=(-123.246,-249.777,0) rot=(0,0,1;5.04173rad)
  Radius = 0.6
FEATURE [Part::Part2DObjectPython] Rectangle061  # Draft 2D object (typed FeaturePython)
  Area = 0
  ChamferSize = 0
  Columns = 1
  FilletRadius = 0
  Height = 6
  Length = 6
  MakeFace = false
  Placement = pos=(-114.365,-251.39,0) rot=(0,0,1;5.12115rad)
  Rows = 1
FEATURE [Part::Part2DObjectPython] Circle061  # Draft 2D object (typed FeaturePython)
  Area = 1.13097
  FirstAngle = 0
  LastAngle = 0
  MakeFace = true
  Placement = pos=(-108.989,-256.253,0) rot=(0,0,1;5.12115rad)
  Radius = 0.6
FEATURE [Part::Part2DObjectPython] Rectangle062  # Draft 2D object (typed FeaturePython)
  Area = 0
  ChamferSize = 0
  Columns = 1
  FilletRadius = 0
  Height = 6
  Length = 6
  MakeFace = false
  Placement = pos=(-100.205,-257.696,0) rot=(0,0,1;5.2517rad)
  Rows = 1
FEATURE [Part::Part2DObjectPython] Circle062  # Draft 2D object (typed FeaturePython)
  Area = 1.13097
  FirstAngle = 0
  LastAngle = 0
  MakeFace = true
  Placement = pos=(-94.2413,-261.819,0) rot=(0,0,1;5.2517rad)
  Radius = 0.6
FEATURE [Part::Part2DObjectPython] Rectangle063  # Draft 2D object (typed FeaturePython)
  Area = 0
  ChamferSize = 0
  Columns = 1
  FilletRadius = 0
  Height = 6
  Length = 6
  MakeFace = false
  Placement = pos=(-50.1281,-273.585,0) rot=(0,0,1;5.85279rad)
  Rows = 1
FEATURE [App::FeaturePython] Text018  # WARN: FeaturePython — macro-defined, semantics opaque (R4)
  Placement = pos=(-53.3517,-270.79,0) rot=(0,0,1;6.25666rad)
  Text = 2
FEATURE [App::FeaturePython] Text019  # WARN: FeaturePython — macro-defined, semantics opaque (R4)
  Placement = pos=(49.5386,-268.047,0) rot=(0,0,1;1.05331rad)
  Text = 3
FEATURE [Part::Part2DObjectPython] Circle063  # Draft 2D object (typed FeaturePython)
  Area = 1.13097
  FirstAngle = 0
  LastAngle = 0
  MakeFace = true
  Placement = pos=(-42.8783,-273.612,0) rot=(0,0,1;5.85279rad)
  Radius = 0.6
FEATURE [Part::Part2DObjectPython] Rectangle064  # Draft 2D object (typed FeaturePython)
  Area = 0
  ChamferSize = 0
  Columns = 1
  FilletRadius = 0
  Height = 6
  Length = 6
  MakeFace = false
  Placement = pos=(-34.4538,-276.509,0) rot=(0,0,1;6.05368rad)
  Rows = 1
FEATURE [Part::Part2DObjectPython] Circle064  # Draft 2D object (typed FeaturePython)
  Area = 1.13097
  FirstAngle = 0
  LastAngle = 0
  MakeFace = true
  Placement = pos=(-27.3444,-275.089,0) rot=(0,0,1;6.05368rad)
  Radius = 0.6
FEATURE [Part::Part2DObjectPython] Rectangle065  # Draft 2D object (typed FeaturePython)
  Area = 0
  ChamferSize = 0
  Columns = 1
  FilletRadius = 0
  Height = 6
  Length = 6
  MakeFace = false
  Placement = pos=(-18.5483,-278.468,0) rot=(0,0,1;6.24985rad)
  Rows = 1
FEATURE [Part::Part2DObjectPython] Circle065  # Draft 2D object (typed FeaturePython)
  Area = 1.13097
  FirstAngle = 0
  LastAngle = 0
  MakeFace = true
  Placement = pos=(-11.852,-275.69,0) rot=(0,0,1;6.24985rad)
  Radius = 0.6
FEATURE [Part::Part2DObjectPython] Rectangle066  # Draft 2D object (typed FeaturePython)
  Area = 0
  ChamferSize = 0
  Columns = 1
  FilletRadius = 0
  Height = 6
  Length = 6
  MakeFace = false
  Placement = pos=(-2.58158,-279.367,0) rot=(0,0,1;0.131249rad)
  Rows = 1
FEATURE [Part::Part2DObjectPython] Circle066  # Draft 2D object (typed FeaturePython)
  Area = 1.13097
  FirstAngle = 0
  LastAngle = 0
  MakeFace = true
  Placement = pos=(3.56904,-275.529,0) rot=(0,0,1;0.131249rad)
  Radius = 0.6
FEATURE [Part::Part2DObjectPython] Rectangle067  # Draft 2D object (typed FeaturePython)
  Area = 0
  ChamferSize = 0
  Columns = 1
  FilletRadius = 0
  Height = 6
  Length = 6
  MakeFace = false
  Placement = pos=(12.7394,-278.834,0) rot=(0,0,1;0.092328rad)
  Rows = 1
FEATURE [Part::Part2DObjectPython] Circle067  # Draft 2D object (typed FeaturePython)
  Area = 1.13097
  FirstAngle = 0
  LastAngle = 0
  MakeFace = true
  Placement = pos=(19.0347,-275.238,0) rot=(0,0,1;0.092328rad)
  Radius = 0.6
FEATURE [Part::Part2DObjectPython] Rectangle068  # Draft 2D object (typed FeaturePython)
  Area = 0
  ChamferSize = 0
  Columns = 1
  FilletRadius = 0
  Height = 6
  Length = 6
  MakeFace = false
  Placement = pos=(33.8505,-271.271,0) rot=(0,0,1;3.14142rad)
  Rows = 1
FEATURE [Part::Part2DObjectPython] Circle068  # Draft 2D object (typed FeaturePython)
  Area = 1.13097
  FirstAngle = 0
  LastAngle = 0
  MakeFace = true
  Placement = pos=(27.25,-274.269,0) rot=(0,0,1;3.14142rad)
  Radius = 0.6
FEATURE [Part::Part2DObjectPython] Rectangle069  # Draft 2D object (typed FeaturePython)
  Area = 0
  ChamferSize = 0
  Columns = 1
  FilletRadius = 0
  Height = 6
  Length = 6
  MakeFace = false
  Placement = pos=(49.1505,-269.111,0) rot=(0,0,1;3.14142rad)
  Rows = 1
FEATURE [Part::Part2DObjectPython] Circle069  # Draft 2D object (typed FeaturePython)
  Area = 1.13097
  FirstAngle = 0
  LastAngle = 0
  MakeFace = true
  Placement = pos=(42.55,-272.109,0) rot=(0,0,1;3.14142rad)
  Radius = 0.6
FEATURE [Part::Part2DObjectPython] Rectangle070  # Draft 2D object (typed FeaturePython)
  Area = 0
  ChamferSize = 0
  Columns = 1
  FilletRadius = 0
  Height = 6
  Length = 6
  MakeFace = false
  Placement = pos=(99.0926,-255.733,0) rot=(0,0,1;3.14072rad)
  Rows = 1
FEATURE [App::FeaturePython] Text020  # WARN: FeaturePython — macro-defined, semantics opaque (R4)
  Placement = pos=(89.1931,-261.188,0) rot=(0,0,-1;5.78612rad)
  Text = 2
FEATURE [App::FeaturePython] Text021  # WARN: FeaturePython — macro-defined, semantics opaque (R4)
  Placement = pos=(176.926,-207.363,0) rot=(0,0,1;1.57691rad)
  Text = 4
FEATURE [Part::Part2DObjectPython] Circle070  # Draft 2D object (typed FeaturePython)
  Area = 1.13097
  FirstAngle = 0
  LastAngle = 0
  MakeFace = true
  Placement = pos=(92.49,-258.727,0) rot=(0,0,1;3.14072rad)
  Radius = 0.6
FEATURE [Part::Part2DObjectPython] Rectangle071  # Draft 2D object (typed FeaturePython)
  Area = 0
  ChamferSize = 0
  Columns = 1
  FilletRadius = 0
  Height = 6
  Length = 6
  MakeFace = false
  Placement = pos=(106.635,-251.033,0) rot=(0,0,1;5.02899rad)
  Rows = 1
FEATURE [Part::Part2DObjectPython] Circle071  # Draft 2D object (typed FeaturePython)
  Area = 1.13097
  FirstAngle = 0
  LastAngle = 0
  MakeFace = true
  Placement = pos=(111.541,-256.371,0) rot=(0,0,1;5.02899rad)
  Radius = 0.6
FEATURE [Part::Part2DObjectPython] Rectangle072  # Draft 2D object (typed FeaturePython)
  Area = 0
  ChamferSize = 0
  Columns = 1
  FilletRadius = 0
  Height = 6
  Length = 6
  MakeFace = false
  Placement = pos=(128.638,-246.019,0) rot=(0,0,1;2.43892rad)
  Rows = 1
FEATURE [Part::Part2DObjectPython] Circle072  # Draft 2D object (typed FeaturePython)
  Area = 1.13097
  FirstAngle = 0
  LastAngle = 0
  MakeFace = true
  Placement = pos=(121.663,-244.043,0) rot=(0,0,1;2.43892rad)
  Radius = 0.6
FEATURE [Part::Part2DObjectPython] Rectangle073  # Draft 2D object (typed FeaturePython)
  Area = 0
  ChamferSize = 0
  Columns = 1
  FilletRadius = 0
  Height = 6
  Length = 6
  MakeFace = false
  Placement = pos=(142.149,-239.907,0) rot=(0,0,1;2.14553rad)
  Rows = 1
FEATURE [Part::Part2DObjectPython] Circle073  # Draft 2D object (typed FeaturePython)
  Area = 1.13097
  FirstAngle = 0
  LastAngle = 0
  MakeFace = true
  Placement = pos=(136.043,-235.998,0) rot=(0,0,1;2.14553rad)
  Radius = 0.6
FEATURE [Part::Part2DObjectPython] Rectangle074  # Draft 2D object (typed FeaturePython)
  Area = 0
  ChamferSize = 0
  Columns = 1
  FilletRadius = 0
  Height = 6
  Length = 6
  MakeFace = false
  Placement = pos=(155.401,-231.025,0) rot=(0,0,1;2.33141rad)
  Rows = 1
FEATURE [Part::Part2DObjectPython] Circle074  # Draft 2D object (typed FeaturePython)
  Area = 1.13097
  FirstAngle = 0
  LastAngle = 0
  MakeFace = true
  Placement = pos=(148.678,-228.312,0) rot=(0,0,1;2.33141rad)
  Radius = 0.6
FEATURE [Part::Part2DObjectPython] Rectangle075  # Draft 2D object (typed FeaturePython)
  Area = 0
  ChamferSize = 0
  Columns = 1
  FilletRadius = 0
  Height = 6
  Length = 6
  MakeFace = false
  Placement = pos=(168.051,-221.504,0) rot=(0,0,1;2.49704rad)
  Rows = 1
FEATURE [Part::Part2DObjectPython] Circle075  # Draft 2D object (typed FeaturePython)
  Area = 1.13097
  FirstAngle = 0
  LastAngle = 0
  MakeFace = true
  Placement = pos=(160.972,-219.937,0) rot=(0,0,1;2.49704rad)
  Radius = 0.6
FEATURE [Part::Part2DObjectPython] Rectangle076  # Draft 2D object (typed FeaturePython)
  Area = 0
  ChamferSize = 0
  Columns = 1
  FilletRadius = 0
  Height = 6
  Length = 6
  MakeFace = false
  Placement = pos=(180.075,-211.331,0) rot=(0,0,1;2.65499rad)
  Rows = 1
FEATURE [Part::Part2DObjectPython] Circle076  # Draft 2D object (typed FeaturePython)
  Area = 1.13097
  FirstAngle = 0
  LastAngle = 0
  MakeFace = true
  Placement = pos=(172.838,-210.897,0) rot=(0,0,1;2.65499rad)
  Radius = 0.6
FEATURE [Part::Part2DObjectPython] Rectangle077  # Draft 2D object (typed FeaturePython)
  Area = 0
  ChamferSize = 0
  Columns = 1
  FilletRadius = 0
  Height = 6
  Length = 6
  MakeFace = false
  Placement = pos=(215.621,-173.061,0) rot=(0,0,1;3.12798rad)
  Rows = 1
FEATURE [App::FeaturePython] Text022  # WARN: FeaturePython — macro-defined, semantics opaque (R4)
  Placement = pos=(207.836,-181.597,0) rot=(0,0,-1;5.26252rad)
  Text = 2
FEATURE [App::FeaturePython] Text023  # WARN: FeaturePython — macro-defined, semantics opaque (R4)
  Placement = pos=(256.902,-91.1209,0) rot=(0,0,1;2.1005rad)
  Text = 5
FEATURE [Part::Part2DObjectPython] Circle077  # Draft 2D object (typed FeaturePython)
  Area = 1.13097
  FirstAngle = 0
  LastAngle = 0
  MakeFace = true
  Placement = pos=(208.98,-175.971,0) rot=(0,0,1;3.12798rad)
  Radius = 0.6
FEATURE [Part::Part2DObjectPython] Rectangle078  # Draft 2D object (typed FeaturePython)
  Area = 0
  ChamferSize = 0
  Columns = 1
  FilletRadius = 0
  Height = 6
  Length = 6
  MakeFace = false
  Placement = pos=(224.612,-160.431,0) rot=(0,0,1;3.29326rad)
  Rows = 1
FEATURE [Part::Part2DObjectPython] Circle078  # Draft 2D object (typed FeaturePython)
  Area = 1.13097
  FirstAngle = 0
  LastAngle = 0
  MakeFace = true
  Placement = pos=(218.541,-164.394,0) rot=(0,0,1;3.29326rad)
  Radius = 0.6
FEATURE [Part::Part2DObjectPython] Rectangle079  # Draft 2D object (typed FeaturePython)
  Area = 0
  ChamferSize = 0
  Columns = 1
  FilletRadius = 0
  Height = 6
  Length = 6
  MakeFace = false
  Placement = pos=(232.944,-147.431,0) rot=(0,0,1;3.42957rad)
  Rows = 1
FEATURE [Part::Part2DObjectPython] Circle079  # Draft 2D object (typed FeaturePython)
  Area = 1.13097
  FirstAngle = 0
  LastAngle = 0
  MakeFace = true
  Placement = pos=(227.468,-152.182,0) rot=(0,0,1;3.42957rad)
  Radius = 0.6
FEATURE [Part::Part2DObjectPython] Rectangle080  # Draft 2D object (typed FeaturePython)
  Area = 0
  ChamferSize = 0
  Columns = 1
  FilletRadius = 0
  Height = 6
  Length = 6
  MakeFace = false
  Placement = pos=(240.533,-134.036,0) rot=(0,0,1;3.56239rad)
  Rows = 1
FEATURE [Part::Part2DObjectPython] Circle080  # Draft 2D object (typed FeaturePython)
  Area = 1.13097
  FirstAngle = 0
  LastAngle = 0
  MakeFace = true
  Placement = pos=(235.734,-139.471,0) rot=(0,0,1;3.56239rad)
  Radius = 0.6
FEATURE [Part::Part2DObjectPython] Rectangle081  # Draft 2D object (typed FeaturePython)
  Area = 0
  ChamferSize = 0
  Columns = 1
  FilletRadius = 0
  Height = 6
  Length = 6
  MakeFace = false
  Placement = pos=(247.354,-120.283,0) rot=(0,0,1;3.69294rad)
  Rows = 1
FEATURE [Part::Part2DObjectPython] Circle081  # Draft 2D object (typed FeaturePython)
  Area = 1.13097
  FirstAngle = 0
  LastAngle = 0
  MakeFace = true
  Placement = pos=(243.303,-126.296,0) rot=(0,0,1;3.69294rad)
  Radius = 0.6
FEATURE [Part::Part2DObjectPython] Rectangle082  # Draft 2D object (typed FeaturePython)
  Area = 0
  ChamferSize = 0
  Columns = 1
  FilletRadius = 0
  Height = 6
  Length = 6
  MakeFace = false
  Placement = pos=(253.39,-106.2,0) rot=(0,0,1;3.82314rad)
  Rows = 1
FEATURE [Part::Part2DObjectPython] Circle082  # Draft 2D object (typed FeaturePython)
  Area = 1.13097
  FirstAngle = 0
  LastAngle = 0
  MakeFace = true
  Placement = pos=(250.154,-112.688,0) rot=(0,0,1;3.82314rad)
  Radius = 0.6
FEATURE [Part::Part2DObjectPython] Rectangle083  # Draft 2D object (typed FeaturePython)
  Area = 0
  ChamferSize = 0
  Columns = 1
  FilletRadius = 0
  Height = 6
  Length = 6
  MakeFace = false
  Placement = pos=(258.592,-91.8496,0) rot=(0,0,1;3.95963rad)
  Rows = 1
FEATURE [Part::Part2DObjectPython] Circle083  # Draft 2D object (typed FeaturePython)
  Area = 1.13097
  FirstAngle = 0
  LastAngle = 0
  MakeFace = true
  Placement = pos=(256.269,-98.7173,0) rot=(0,0,1;3.95963rad)
  Radius = 0.6
FEATURE [App::DocumentObjectGroup] Everything
  Group = -> [Rectangle,Circle,Rectangle001,Circle001,Rectangle002,Circle002,Rectangle003,Circle003,Rectangle004,Circle004,Rectangle005,Circle005,Rectangle006,Circle006,Rectangle007,Circle007,Rectangle008,Circle008,Rectangle009,Circle009,Rectangle010,Circle010,Rectangle011,Circle011,Rectangle012,Circle012,Rectangle013,Circle013,Rectangle014,Circle014,Rectangle015,Circle015,Rectangle016,Circle016,Rectangle017,+133 more]
